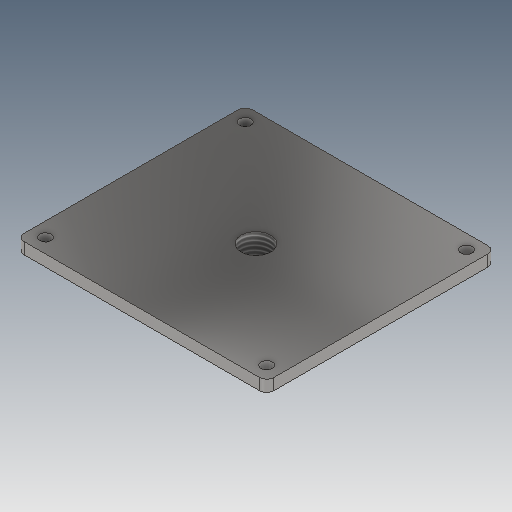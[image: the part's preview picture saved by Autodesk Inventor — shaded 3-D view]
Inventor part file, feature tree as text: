
AUTODESK INVENTOR PART (.ipt)
format: ipt  version: 2025 (Build 290162000, 162)  size: 371,712 bytes
history: native  units: mm
features: sketch x5, extrude x3, fillet x2, hole x1
ambient origin geometry x8: Origin, YZ Plane, XZ Plane, XY Plane, X Axis, Y Axis, Z Axis, Center Point
bodies: 实体1 (feature_tree)
feature tree (11):
  sketch  "草图1"  dims[d4=8.0mm d0=160.0mm]
  extrude  "拉伸1"  Depth=160.0mm
  extrude  "拉伸2"  Depth=8.0mm
  fillet  "圆角1"  Radius=20.0mm
  extrude  "拉伸3"  Depth=5.0mm
  fillet  "圆角2"  Radius=8.0mm
  hole  "孔2"  [1 undecoded]
  sketch  "草图 - 矩形阵列1"  dims[d1=175.0mm d2=8.0mm d3=20.0mm d6=140.0mm]
  sketch  "草图2"  dims[d7=20.0mm d9=155.0mm d12=5.0mm d13=8.0mm]
  sketch  "草图3"  dims[d14=0.0mm d15=5.0mm]
  sketch  "草图4"  dims[d16=120.0mm d17=135.0mm d18=1.5mm d19=0.0mm d20=2.0mm d28=32.0mm d29=8.5mm d30=0.0mm d31=2.0mm d32=20.752mm d33=48.0mm d34=4.0mm d35=2.0mm d36=90.0deg d37=8.0mm d38=120.0deg]
note: 1 required parameter value undecoded (feature->parameter linkage not recoverable at this tier; creation-order binding heuristic only, values carry confidence <= 0.55)
